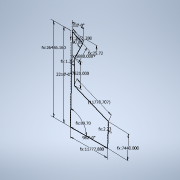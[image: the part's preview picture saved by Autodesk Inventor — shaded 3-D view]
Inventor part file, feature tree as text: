
AUTODESK INVENTOR PART (.ipt)
format: ipt  version: 2021 (Build 250183000, 183)  size: 107,520 bytes
history: native  units: in
note: dims shown in document units (in); Inventor stores cm internally (conversion verified against a paired STEP export)
features: sketch x1
ambient origin geometry x8: Origin, YZ Plane, XZ Plane, XY Plane, X Axis, Y Axis, Z Axis, Center Point
feature tree (1):
  sketch  "Sketch1"  dims[d0=26520.0in d1=11784.0in d2=0.0088in d3=26486.16in d4=11777.88in d5=0.6164in d6=3720.0in d7=0.1767in d8=90.0deg d9=5880.0in d10=7620.0in d12=7440.0in d13=0.0153in d16=3665.28in d17=11778.7072in]
